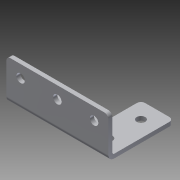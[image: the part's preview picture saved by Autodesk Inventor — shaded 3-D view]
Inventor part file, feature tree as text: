
AUTODESK INVENTOR PART (.ipt)
format: ipt  version: 2013 (Build 170138000, 138)  size: 218,112 bytes
history: native  units: in
note: dims shown in document units (in); Inventor stores cm internally (conversion verified against a paired STEP export)
features: sheet_metal_op x4, other x4, sketch x3, chamfer x1
ambient origin geometry x8: Origin, YZ Plane, XZ Plane, XY Plane, X Axis, Y Axis, Z Axis, Center Point
feature tree (12):
  sheet_metal_op  "Face1"
  sheet_metal_op  "Flange1"
  chamfer  "Corner Round1"
  sketch  "Sketch1"  dims[d0=2.0in]
  other  "Plate1"
  sketch  "Sketch2"  dims[d1=1.0in]
  other  "Plate2"
  sheet_metal_op  "Bend1"
  sheet_metal_op  "Corner1"
  sketch  "Sketch3"  dims[d2=0.26in d3=0.26in d4=1.0in d8=0.125in d9=0.125in d10=0.0625in d11=0.25in d12=0.125in d13=1.25in d14=90.0deg d15=0.05in d16=0.5in d17=0.125in d18=0.125in d19=0.26in d22=0.125in d23=0.0in d24=0.125in d25=2.125in d26=2.25in d27=0.75in d28=0.875in d29=2.25in d5=0.125in d6=0.0in d7=0.25in]
  other  "Cut1"
  other  "Definition1"
